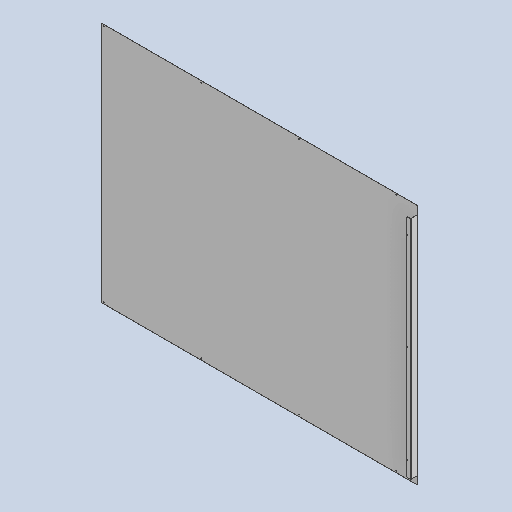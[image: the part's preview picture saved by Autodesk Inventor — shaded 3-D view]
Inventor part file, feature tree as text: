
AUTODESK INVENTOR PART (.ipt)
format: ipt  version: 2025 (Build 290162010, 162A)  size: 242,176 bytes
history: native  units: mm
features: sheet_metal_op x7, other x4, sketch x4, extrude x2, pattern_linear x2, projected_geometry x2, chamfer x1
ambient origin geometry x8: Origin, YZ Plane, XZ Plane, XY Plane, X Axis, Y Axis, Z Axis, Center Point
bodies: Solid1 (feature_tree)
feature tree (22):
  sheet_metal_op  "Face1"
  sheet_metal_op  "Flange1"
  sheet_metal_op  "Flange2"
  extrude  "Extrusion4"  Depth=1490.0mm
  pattern_linear  "Rectangular Pattern6"  Spacing1=1.6mm  [1 undecoded]
  extrude  "Extrusion5"  Depth=0.8mm
  pattern_linear  "Rectangular Pattern7"  Spacing1=41.0mm  [1 undecoded]
  chamfer  "Corner Round1"
  other  "Plate1"
  sketch  "Sketch5"  dims[d0=1945.0mm d1=1490.0mm]
  other  "Plate2"
  sheet_metal_op  "Bend1"
  sheet_metal_op  "Corner1"
  sketch  "Sketch6"  dims[d2=0.8mm]
  other  "Plate3"
  sheet_metal_op  "Bend2"
  sheet_metal_op  "Corner2"
  sketch  "Sketch8"  dims[d50=0.8mm]
  projected_geometry  "Projected Loop3"
  sketch  "Sketch9"  dims[d51=0.4mm d52=1.6mm d53=0.8mm d54=41.0mm d55=90.0deg d56=0.8mm d57=3.2mm d58=0.8mm d59=0.8mm d60=0.8mm d61=0.4mm d62=1.6mm d63=0.8mm d64=25.0mm d65=14.835299mm d66=0.8mm d67=3.2mm d68=0.8mm d69=0.8mm d80=50.0mm d81=50.0mm d82=5.0mm d83=18.0mm d84=0.8mm d85=0.0mm d86=30.0mm d88=600.0mm d89=10.0mm d90=6.0mm d91=15.0mm d92=0.8mm d93=0.0mm d94=40.0mm d96=600.0mm d97=6.0mm d98=0.5mm d99=0.872665mm]
  projected_geometry  "Projected Loop4"
  other  "Definition1"
note: 2 required parameter values undecoded (feature->parameter linkage not recoverable at this tier; creation-order binding heuristic only, values carry confidence <= 0.55)
